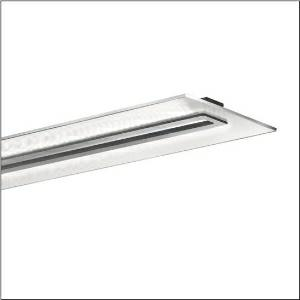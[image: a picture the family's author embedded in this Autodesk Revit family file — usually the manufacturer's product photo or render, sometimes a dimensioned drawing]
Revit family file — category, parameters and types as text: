
# Revit family: vega_r__11_5mn238dlc_e876
name_source: partatom
category: Lighting Fixtures
units: mm (PartAtom-declared; Revit-internal decimal feet)

## family parameters
Cut with Voids When Loaded = No
Host = Face
Light Source = No
Part Type = Normal
Room Calculation Point = No
Round Connector Dimension = Use Diameter
Shared = No

## types (1)
- --- (1 x LED 4000K / CRI = 80 (unbekannt), 4300 lm, 4000K)
    Apparent Load = 31 VA
    CIE Flux Codes = 61 86 97 62 100
    Color Rendering = 80
    Color Temperature = 4000K
    Default Elevation = 1800 mm
    Description = Vega® 11, office luminaire, primary light control with prismatic reflector, of PMMA, transparent prismatic structure, CAT 2 (L<= 1500cd/m²), light emission: direct/indirect distribution, primary light characteristic: symmetric, installation type: suspended mounting, surface-mounted, LED, rated luminous flux: 4.300lm, luminous efficacy: 139lm/W, light colour: 840, colour temperature: 4000K, control gear: DALI, with terminal, 3+2-pole, max. 2.5mm², mains connection: 230V, AC, 50Hz, connection cable inclusive, cable length: 1,5m, rated input power: 31W, luminaire housing, rectangular, rounded, of aluminium section, anodised, metallic grey (RAL 9006), length: 1.250mm, width: 350mm, height: 43mm, luminaire housing, lower part, of aluminium section, anodised, metallic grey (RAL 9006), of PC, grey, protection rating (complete): IP20, insulation class (complete): insulation class I (protective earthing), certification: CE, standard: EN 50419, packaging unit: 1 piece
    Height = 40 mm  [stored 0.131234 ft]
    Lamp = 1 x LED 4000K / CRI >= 80 (unbekannt)
    Lamp Light Flux = 4300 lm
    Lamp count = 1
    Length = 1250 mm
    Luminous efficacy = 139 lm/W
    Manufacturer = Siteco
    ModVariant = No
    Model = 5MN238DLC
    Mounting Place = Ceiling
    Mounting Type = Pendant
    Number of Poles = 1
    OnlyDefault = Yes
    Power Factor = 1
    Product Name = Vega® 11
    Product group = office luminaire | ceiling pendant
    ProductGroupID = 904
    Protection Class = Protection class I
    Protection Degree = IP 20
    RLX_Detail_Level = 1
    RLX_Emergency_Light_Flux = 0 lm
    RLX_Emergency_Type = 0
    RLX_Emergency_Type_DB = No
    RlxData = <blob elided: 62973 chars, md5=c882aadf>
    Socket = socket
    Standby Power = 0 W
    System Light Flux = 4300 lm
    System Power = 31 W
    Type Comments = factory setting: luminous flux: 100 % | dim-lin: 254 | 231 mA
    Type Image = l_1004807.jpg
    URL = http://relux.com
    VarID = @adj_203812
    Voltage = 0 V
    Weight = 0.00 kg
    Width = 350 mm

note: [stored X ft] marks values corroborated as IEEE doubles in the binary element streams (Revit-internal decimal feet)

## geometry (parser evidence)
native form markers: Blend x4, Sweep x11
no freeform markers — native parametric forms only
